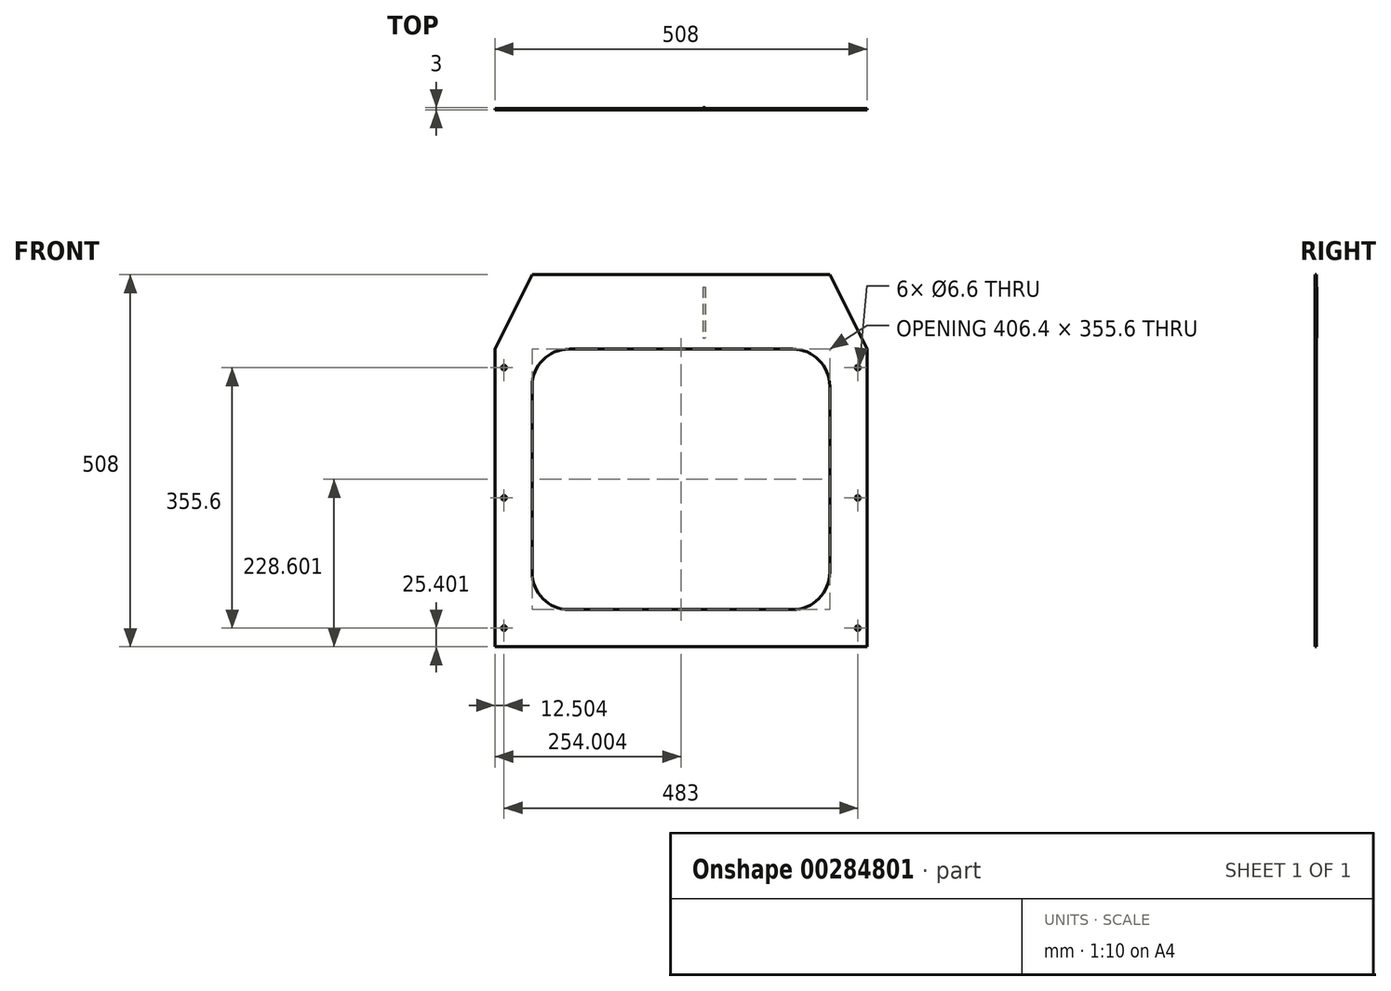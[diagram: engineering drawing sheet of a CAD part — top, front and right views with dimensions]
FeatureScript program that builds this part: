
annotation { "Feature Type Name" : "Feature", "Feature Type Description" : "" }
export const myFeature = defineFeature(function(context is Context, id is Id, definition is map)
    precondition{}
    {
        {
            var Q0;
            Q0=qCreatedBy(makeId("Front.planeOp"),FACE);
            var sketch = newSketch(context, id + "F0", { "sketchPlane" : qUnion([Q0])});
            skLineSegment(sketch, "E0.bottom", {"start": v(-307.35, -195.99) * mm, "end": v(200.65, -195.99) * mm});
            skLineSegment(sketch, "E0.left", {"start": v(-307.35, -195.99) * mm, "end": v(-307.35, 210.41) * mm});
            skLineSegment(sketch, "E0.right", {"start": v(200.65, -195.99) * mm, "end": v(200.65, 210.41) * mm});
            skLineSegment(sketch, "E1", {"start": v(-307.35, 210.41) * mm, "end": v(-256.55, 312.01) * mm});
            skLineSegment(sketch, "E2", {"start": v(-256.55, 312.01) * mm, "end": v(149.85, 312.01) * mm});
            skLineSegment(sketch, "E3", {"start": v(149.85, 312.01) * mm, "end": v(200.65, 210.41) * mm});
            skSolve(sketch);
        }
        {
            var Q0;
            Q0 = qSketchRegion(id + "F0", true);
            extrude(context, id + "F1", {"entities" : qUnion([Q0]), "depth" : 2 * mm});
        }
        {
            var Q0;
            Q0=makeQuery(id+"F1.opExtrude","CAP_FACE",FACE,{"disambiguationData":[OSD([sQuery(id+"F0.wireOp",EDGE,"E0.bottom"),sQuery(id+"F0.wireOp",EDGE,"E0.left"),sQuery(id+"F0.wireOp",EDGE,"E0.right"),sQuery(id+"F0.wireOp",EDGE,"E1"),sQuery(id+"F0.wireOp",EDGE,"E2"),sQuery(id+"F0.wireOp",EDGE,"E3")])],"isStart":false});
            var sketch = newSketch(context, id + "F2", { "sketchPlane" : qUnion([Q0])});
            skLineSegment(sketch, "E4.bottom", {"start": v(-205.75, 210.41) * mm, "end": v(99.05, 210.41) * mm});
            skLineSegment(sketch, "E4.top", {"start": v(-205.75, -145.19) * mm, "end": v(99.05, -145.19) * mm});
            skLineSegment(sketch, "E4.left", {"start": v(-256.55, 159.61) * mm, "end": v(-256.55, -94.39) * mm});
            skLineSegment(sketch, "E4.right", {"start": v(149.85, 159.61) * mm, "end": v(149.85, -94.39) * mm});
            skPoint(sketch, "E5.visualSharp", {"position": v(-256.55, 210.41) * mm});
            skArc(sketch, "E5.filletArc", {"start": v(-205.75, 210.41) * mm, "mid": v(-241.67, 195.53) * mm, "end": v(-256.55, 159.61) * mm});
            skPoint(sketch, "E6.visualSharp", {"position": v(149.85, 210.41) * mm});
            skArc(sketch, "E6.filletArc", {"start": v(149.85, 159.61) * mm, "mid": v(134.97, 195.53) * mm, "end": v(99.05, 210.41) * mm});
            skPoint(sketch, "E7.visualSharp", {"position": v(149.85, -145.19) * mm});
            skArc(sketch, "E7.filletArc", {"start": v(99.05, -145.19) * mm, "mid": v(134.97, -130.3) * mm, "end": v(149.85, -94.39) * mm});
            skPoint(sketch, "E8.visualSharp", {"position": v(-256.55, -145.19) * mm});
            skArc(sketch, "E8.filletArc", {"start": v(-256.55, -94.39) * mm, "mid": v(-241.67, -130.3) * mm, "end": v(-205.75, -145.19) * mm});
            skSolve(sketch);
        }
        {
            var Q0;
            Q0 = qSketchRegion(id + "F2", true);
            extrude(context, id + "F3", {"entities" : qUnion([Q0]), "operationType" : NewBodyOperationType.REMOVE, "endBound" : BoundingType.THROUGH_ALL, "oppositeDirection" : true, "depth" : 25 * mm});
        }
        {
            var Q0;
            {var subQ0=sQuery(id+"F0.wireOp",EDGE,"E3");var subQ1=sQuery(id+"F0.wireOp",EDGE,"E0.bottom");var subQ2=sQuery(id+"F0.wireOp",EDGE,"E2");var subQ3=sQuery(id+"F0.wireOp",EDGE,"E1");var subQ4=sQuery(id+"F0.wireOp",EDGE,"E0.left");var subQ5=sQuery(id+"F0.wireOp",EDGE,"E0.right");Q0=makeQuery(id+"F3.boolean.opBoolean","SPLIT",FACE,{"disambiguationData":[TD([makeQuery(id+"F1.opExtrude","SWEPT_FACE",FACE,{"disambiguationData":[OSD([subQ1])]})])],"derivedFrom":makeQuery(id+"F1.opExtrude","CAP_FACE",FACE,{"disambiguationData":[OSD([subQ1,subQ4,subQ5,subQ3,subQ2,subQ0])],"isStart":false})});}
            var sketch = newSketch(context, id + "F4", { "sketchPlane" : qUnion([Q0])});
            skLineSegment(sketch, "E9.bottom", {"start": v(-22.97, 295.25) * mm, "end": v(-19.97, 295.25) * mm});
            skLineSegment(sketch, "E9.top", {"start": v(-22.97, 225.47) * mm, "end": v(-19.97, 225.47) * mm});
            skLineSegment(sketch, "E9.left", {"start": v(-22.97, 295.25) * mm, "end": v(-22.97, 225.47) * mm});
            skLineSegment(sketch, "E9.right", {"start": v(-19.97, 295.25) * mm, "end": v(-19.97, 225.47) * mm});
            skSolve(sketch);
        }
        {
            var Q0;
            Q0 = qSketchRegion(id + "F4", true);
            extrude(context, id + "F5", {"entities" : qUnion([Q0]), "operationType" : NewBodyOperationType.ADD, "oppositeDirection" : true, "depth" : 3 * mm});
        }
        {
            var Q0;
            {var subQ0=sQuery(id+"F0.wireOp",EDGE,"E3");var subQ1=sQuery(id+"F0.wireOp",EDGE,"E2");var subQ2=sQuery(id+"F0.wireOp",EDGE,"E1");var subQ3=sQuery(id+"F0.wireOp",EDGE,"E0.right");var subQ4=sQuery(id+"F0.wireOp",EDGE,"E0.left");var subQ5=sQuery(id+"F0.wireOp",EDGE,"E0.bottom");var subQ6=makeQuery(id+"F1.opExtrude","CAP_FACE",FACE,{"disambiguationData":[OSD([subQ5,subQ4,subQ3,subQ2,subQ1,subQ0])],"isStart":false});Q0=makeQuery(id+"F5.boolean.opBoolean","MERGE",FACE,{"derivedFrom":[makeQuery(id+"F3.boolean.opBoolean","SPLIT",FACE,{"disambiguationData":[TD([makeQuery(id+"F1.opExtrude","SWEPT_FACE",FACE,{"disambiguationData":[OSD([subQ5])]})])],"derivedFrom":subQ6}),makeQuery(id+"F3.boolean.opBoolean","SPLIT",FACE,{"disambiguationData":[TD([makeQuery(id+"F3.opExtrude","SWEPT_FACE",FACE,{"disambiguationData":[OSD([sQuery(id+"F2.wireOp",EDGE,"37a97e87-8427-4c95-81a0-ebdeb4e0e8c7.sketch_text.stroke-54")])]})])],"derivedFrom":subQ6}),makeQuery(id+"F5.opExtrude","CAP_FACE",FACE,{"disambiguationData":[OSD([sQuery(id+"F4.wireOp",EDGE,"E9.bottom"),sQuery(id+"F4.wireOp",EDGE,"E9.top"),sQuery(id+"F4.wireOp",EDGE,"E9.left"),sQuery(id+"F4.wireOp",EDGE,"E9.right")])],"isStart":true})]});}
            var sketch = newSketch(context, id + "F6", { "sketchPlane" : qUnion([Q0])});
            skPoint(sketch, "E10", {"position": v(-294.85, 185.01) * mm});
            skPoint(sketch, "E11", {"position": v(-294.85, 7.21) * mm});
            skPoint(sketch, "E12", {"position": v(-294.85, -170.59) * mm});
            skPoint(sketch, "E13", {"position": v(188.15, 185.01) * mm});
            skPoint(sketch, "E14", {"position": v(188.15, 7.21) * mm});
            skPoint(sketch, "E15", {"position": v(188.15, -170.59) * mm});
            skSolve(sketch);
        }
        {
            var Q0;
            Q0=sQuery(id+"F6.wireOp",VERTEX,"E10");
            var Q1;
            Q1=sQuery(id+"F6.wireOp",VERTEX,"E11");
            var Q2;
            Q2=sQuery(id+"F6.wireOp",VERTEX,"E12");
            var Q3;
            Q3=sQuery(id+"F6.wireOp",VERTEX,"E15");
            var Q4;
            Q4=sQuery(id+"F6.wireOp",VERTEX,"E14");
            var Q5;
            Q5=sQuery(id+"F6.wireOp",VERTEX,"E13");
            var Q6;
            Q6=makeQuery(id+"F3.boolean.opBoolean","SPLIT",BODY,{"disambiguationData":[OD(0.0)],"derivedFrom":makeQuery(id+"F1.opExtrude","SWEPT_BODY",BODY,{"disambiguationData":[OSD([sQuery(id+"F0.wireOp",EDGE,"E0.bottom"),sQuery(id+"F0.wireOp",EDGE,"E0.left"),sQuery(id+"F0.wireOp",EDGE,"E0.right"),sQuery(id+"F0.wireOp",EDGE,"E1"),sQuery(id+"F0.wireOp",EDGE,"E2"),sQuery(id+"F0.wireOp",EDGE,"E3")])]})});
            hole(context, id + "F7", {"style" : HoleStyle.SIMPLE, "endStyle" : HoleEndStyle.THROUGH, "standardTappedOrClearance" : lookupTablePath({ "standard" : "ISO", "fit" : "Normal", "size" : "M6", "type" : "Clearance" }), "standardBlindInLast" : lookupTablePath({ "fit" : "Standard", "standard" : "ISO", "size" : "M6", "type" : "Clearance" }), "holeDiameter" : 6.6 * mm, "tappedDepth" : 12 * mm, "tapClearance" : 3, "locations" : qUnion([Q0, Q1, Q2, Q3, Q4, Q5]), "scope" : qUnion([Q6])});
        }
    });
